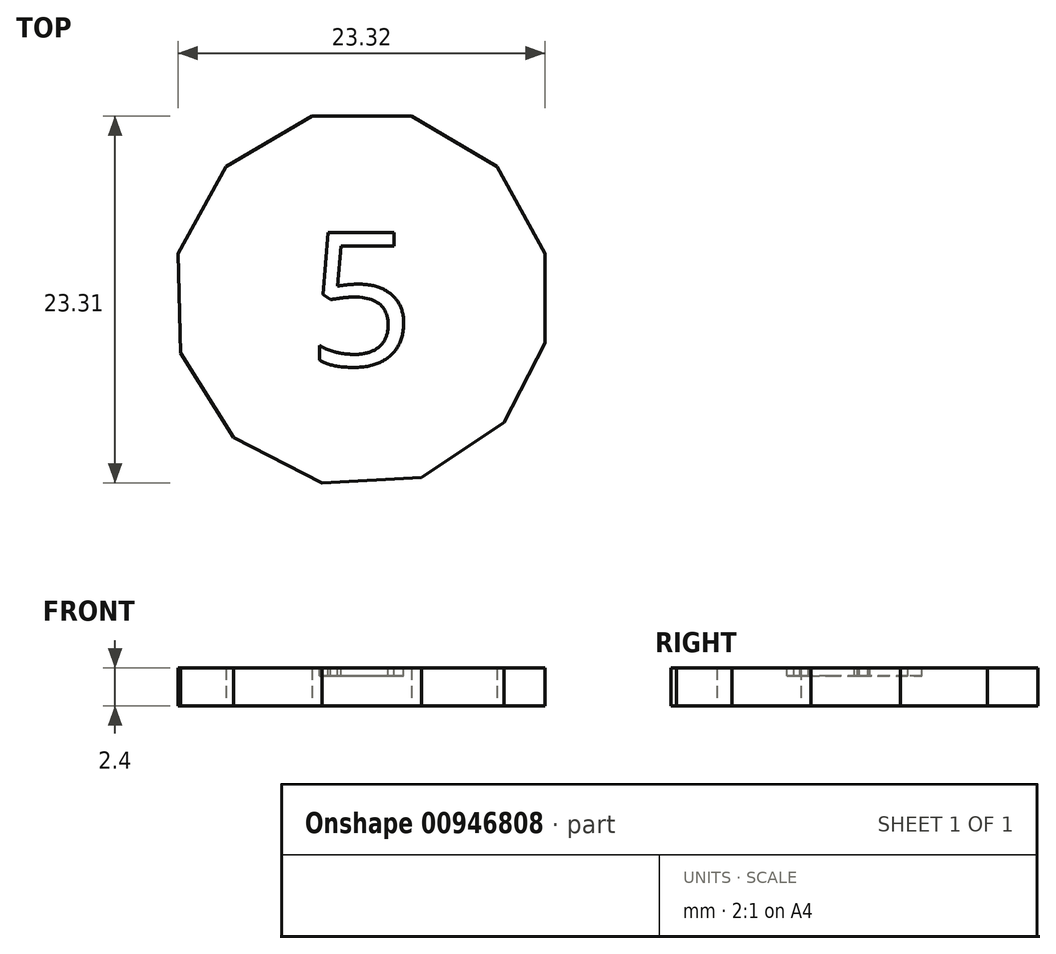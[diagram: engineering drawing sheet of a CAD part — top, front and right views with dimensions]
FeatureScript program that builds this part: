
annotation { "Feature Type Name" : "Feature", "Feature Type Description" : "" }
export const myFeature = defineFeature(function(context is Context, id is Id, definition is map)
    precondition{}
    {
        {
            var Q0;
            Q0=qCreatedBy(makeId("Top.planeOp"),FACE);
            var sketch = newSketch(context, id + "F0", { "sketchPlane" : qUnion([Q0])});
            skCircle(sketch, "E0", {"center": v(0, 0) * mm, "radius": 12 * mm, "construction": true});
            skLineSegment(sketch, "E1", {"start": v(-3.16, 11.58) * mm, "end": v(3.16, 11.58) * mm});
            skLineSegment(sketch, "E2", {"start": v(3.16, 11.58) * mm, "end": v(8.6, 8.37) * mm});
            skLineSegment(sketch, "E3", {"start": v(8.6, 8.37) * mm, "end": v(11.66, 2.84) * mm});
            skLineSegment(sketch, "E4", {"start": v(11.66, 2.84) * mm, "end": v(11.66, -2.84) * mm});
            skLineSegment(sketch, "E5", {"start": v(11.66, -2.84) * mm, "end": v(9.05, -7.88) * mm});
            skLineSegment(sketch, "E6", {"start": v(9.05, -7.88) * mm, "end": v(3.8, -11.39) * mm});
            skLineSegment(sketch, "E7", {"start": v(3.8, -11.39) * mm, "end": v(-2.52, -11.73) * mm});
            skLineSegment(sketch, "E8", {"start": v(-2.52, -11.73) * mm, "end": v(-8.13, -8.83) * mm});
            skLineSegment(sketch, "E9", {"start": v(-8.13, -8.83) * mm, "end": v(-11.49, -3.48) * mm});
            skLineSegment(sketch, "E10", {"start": v(-11.49, -3.48) * mm, "end": v(-11.66, 2.84) * mm});
            skLineSegment(sketch, "E11", {"start": v(-11.66, 2.84) * mm, "end": v(-8.6, 8.37) * mm});
            skLineSegment(sketch, "E12", {"start": v(-8.6, 8.37) * mm, "end": v(-3.16, 11.58) * mm});
            skLineSegment(sketch, "E13", {"start": v(-3.16, 11.58) * mm, "end": v(0, 0) * mm, "construction": true});
            skLineSegment(sketch, "E14", {"start": v(3.16, 11.58) * mm, "end": v(0, 0) * mm, "construction": true});
            skLineSegment(sketch, "E15", {"start": v(8.6, 8.37) * mm, "end": v(0, 0) * mm, "construction": true});
            skLineSegment(sketch, "E16", {"start": v(11.66, 2.84) * mm, "end": v(0, 0) * mm, "construction": true});
            skLineSegment(sketch, "E17", {"start": v(11.66, -2.84) * mm, "end": v(0, 0) * mm, "construction": true});
            skLineSegment(sketch, "E18", {"start": v(0, 0) * mm, "end": v(9.05, -7.88) * mm, "construction": true});
            skLineSegment(sketch, "E19", {"start": v(0, 0) * mm, "end": v(3.8, -11.39) * mm, "construction": true});
            skLineSegment(sketch, "E20", {"start": v(0, 0) * mm, "end": v(-2.52, -11.73) * mm, "construction": true});
            skLineSegment(sketch, "E21", {"start": v(0, 0) * mm, "end": v(-8.13, -8.83) * mm, "construction": true});
            skLineSegment(sketch, "E22", {"start": v(-11.49, -3.48) * mm, "end": v(0, 0) * mm, "construction": true});
            skLineSegment(sketch, "E23", {"start": v(0, 0) * mm, "end": v(-11.66, 2.84) * mm, "construction": true});
            skLineSegment(sketch, "E24", {"start": v(-8.6, 8.37) * mm, "end": v(0, 0) * mm, "construction": true});
            skSolve(sketch);
        }
        {
            var Q0;
            Q0=makeQuery(id+"F0.imprint","IMPRINT",FACE,{"disambiguationData":[TD([[makeQuery(id+"F0.imprint","IMPRINT",EDGE,{"derivedFrom":sQuery(id+"F0.wireOp",EDGE,"E1")}),-1.0]])]});
            extrude(context, id + "F1", {"entities" : qUnion([Q0]), "depth" : 2.4 * mm, "offsetDistance" : 25 * mm});
        }
        {
            var Q0;
            Q0=makeQuery(id+"F1.opExtrude","CAP_FACE",FACE,{"disambiguationData":[OSD([sQuery(id+"F0.wireOp",EDGE,"E1"),sQuery(id+"F0.wireOp",EDGE,"E2"),sQuery(id+"F0.wireOp",EDGE,"E3"),sQuery(id+"F0.wireOp",EDGE,"E4"),sQuery(id+"F0.wireOp",EDGE,"E5"),sQuery(id+"F0.wireOp",EDGE,"E6"),sQuery(id+"F0.wireOp",EDGE,"E7"),sQuery(id+"F0.wireOp",EDGE,"E8"),sQuery(id+"F0.wireOp",EDGE,"E9"),sQuery(id+"F0.wireOp",EDGE,"E10"),sQuery(id+"F0.wireOp",EDGE,"E11"),sQuery(id+"F0.wireOp",EDGE,"E12")])],"isStart":false});
            var sketch = newSketch(context, id + "F2", { "sketchPlane" : qUnion([Q0])});
            skText(sketch, "E25", { "text": "5", "fontName": "OpenSans-Regular.ttf"});
            skLineSegment(sketch, "E26", {"start": v(-3.43, 4.27) * mm, "end": v(3.43, -4.27) * mm, "construction": true});
            skLineSegment(sketch, "E27", {"start": v(3.43, 4.27) * mm, "end": v(-3.43, -4.27) * mm, "construction": true});
            skPoint(sketch, "E28", {"position": v(0, 0) * mm});
            const initialGuessF2  = {"E25": [-0.00343, -0.00427, 1, 0, 0.00854]};
            skSetInitialGuess(sketch, initialGuessF2);
            skSolve(sketch);
        }
        {
            var Q0;
            Q0 = qSketchRegion(id + "F2", true);
            extrude(context, id + "F3", {"entities" : qUnion([Q0]), "operationType" : NewBodyOperationType.REMOVE, "oppositeDirection" : true, "depth" : .5 * mm, "offsetDistance" : 25 * mm});
        }
    });
